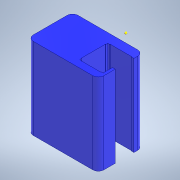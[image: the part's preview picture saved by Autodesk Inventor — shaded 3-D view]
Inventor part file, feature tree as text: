
AUTODESK INVENTOR PART (.ipt)
format: ipt  version: 2022 (Build 260153000, 153)  size: 230,912 bytes
history: native  units: mm
features: extrude x7, sketch x7, hole x2, projected_geometry x2, plane x1, thicken_offset x1, fillet x1
ambient origin geometry x8: Origin, YZ Plane, XZ Plane, XY Plane, X Axis, Y Axis, Z Axis, Center Point
bodies: Solid1 (feature_tree)
feature tree (21):
  extrude  "Extrusion1"  Depth=44.0mm TaperAngle=0.0deg
  sketch  "Sketch2"  dims[d3=44.0mm d4=35.0mm d5=0.0mm]
  extrude  "Extrusion2"  Depth=10.0mm
  hole  "Hole2"  [1 undecoded]
  plane  "Work Plane1"
  extrude  "Extrusion6"  Depth=5.0mm TaperAngle=0.0deg
  thicken_offset  "Thicken1"
  extrude  "Extrusion7"  Depth=0.1mm
  extrude  "Extrusion8"  Depth=3.0mm
  hole  "Hole3"  [1 undecoded]
  extrude  "Extrusion9"  Depth=3.0mm
  extrude  "Extrusion10"  Depth=3.0mm
  fillet  "Fillet1"  Radius=1.0mm
  sketch  "Sketch12"  dims[d45=1.0mm d46=1.0mm d47=0.2mm d48=0.2mm d49=1.0mm d50=1.0mm d51=0.2mm d52=0.0mm d53=0.0mm d54=1.5mm d55=10.0mm d56=0.0mm d57=24.03mm d59=8.5mm d60=10.0mm d61=9.382mm d62=22.0mm d63=4.0mm d64=6.0mm d65=6.3mm d66=2.0mm d67=90.0deg d68=10.0mm d69=0.0mm d70=5.0mm d71=5.0mm d72=5.0mm d73=4.0mm d74=0.0mm d75=0.0mm d76=0.0mm d77=0.0mm d78=3.0mm]
  sketch  "Sketch6"  dims[d6=10.0mm d7=10.0mm]
  projected_geometry  "Projected Loop2"
  sketch  "Sketch7"  dims[d8=16.6mm d9=0.0mm]
  sketch  "Sketch8"  dims[d20=4.0mm d21=6.0mm d22=4.0mm d23=2.0mm d24=90.0deg d25=10.0mm d26=0.0mm d30=4.0mm]
  sketch  "Sketch10"  dims[d40=4.0mm d41=5.0mm d42=0.0mm]
  sketch  "Sketch11"  dims[d43=0.1mm d44=0.1mm]
  projected_geometry  "Projected Loop3"
note: 2 required parameter values undecoded (feature->parameter linkage not recoverable at this tier; creation-order binding heuristic only, values carry confidence <= 0.55)
